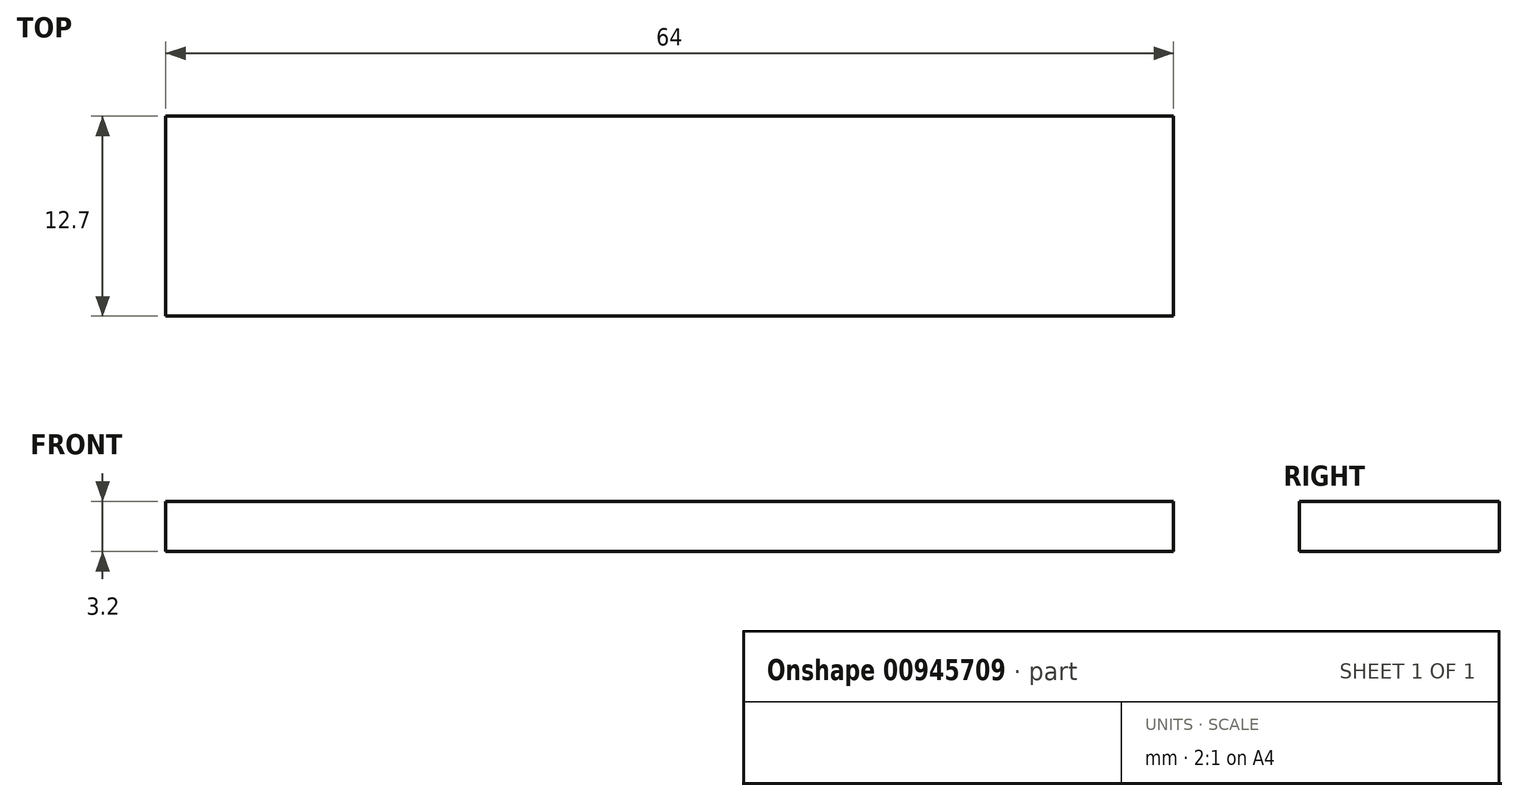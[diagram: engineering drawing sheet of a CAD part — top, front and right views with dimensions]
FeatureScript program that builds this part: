
annotation { "Feature Type Name" : "Feature", "Feature Type Description" : "" }
export const myFeature = defineFeature(function(context is Context, id is Id, definition is map)
    precondition{}
    {
        {
            var Q0;
            Q0=qCreatedBy(makeId("Top.planeOp"),FACE);
            var sketch = newSketch(context, id + "F0", { "sketchPlane" : qUnion([Q0])});
            skLineSegment(sketch, "E0.bottom", {"start": v(0, 0) * mm, "end": v(64, 0) * mm});
            skLineSegment(sketch, "E0.top", {"start": v(0, 12.7) * mm, "end": v(64, 12.7) * mm});
            skLineSegment(sketch, "E0.left", {"start": v(0, 0) * mm, "end": v(0, 12.7) * mm});
            skLineSegment(sketch, "E0.right", {"start": v(64, 0) * mm, "end": v(64, 12.7) * mm});
            skSolve(sketch);
        }
        {
            var Q0;
            Q0=makeQuery(id+"F0.imprint","IMPRINT",FACE,{"disambiguationData":[TD([[makeQuery(id+"F0.imprint","IMPRINT",EDGE,{"derivedFrom":sQuery(id+"F0.wireOp",EDGE,"E0.bottom")}),1.0]])]});
            extrude(context, id + "F1", {"entities" : qUnion([Q0]), "depth" : 3.2 * mm, "offsetDistance" : 25 * mm});
        }
    });
